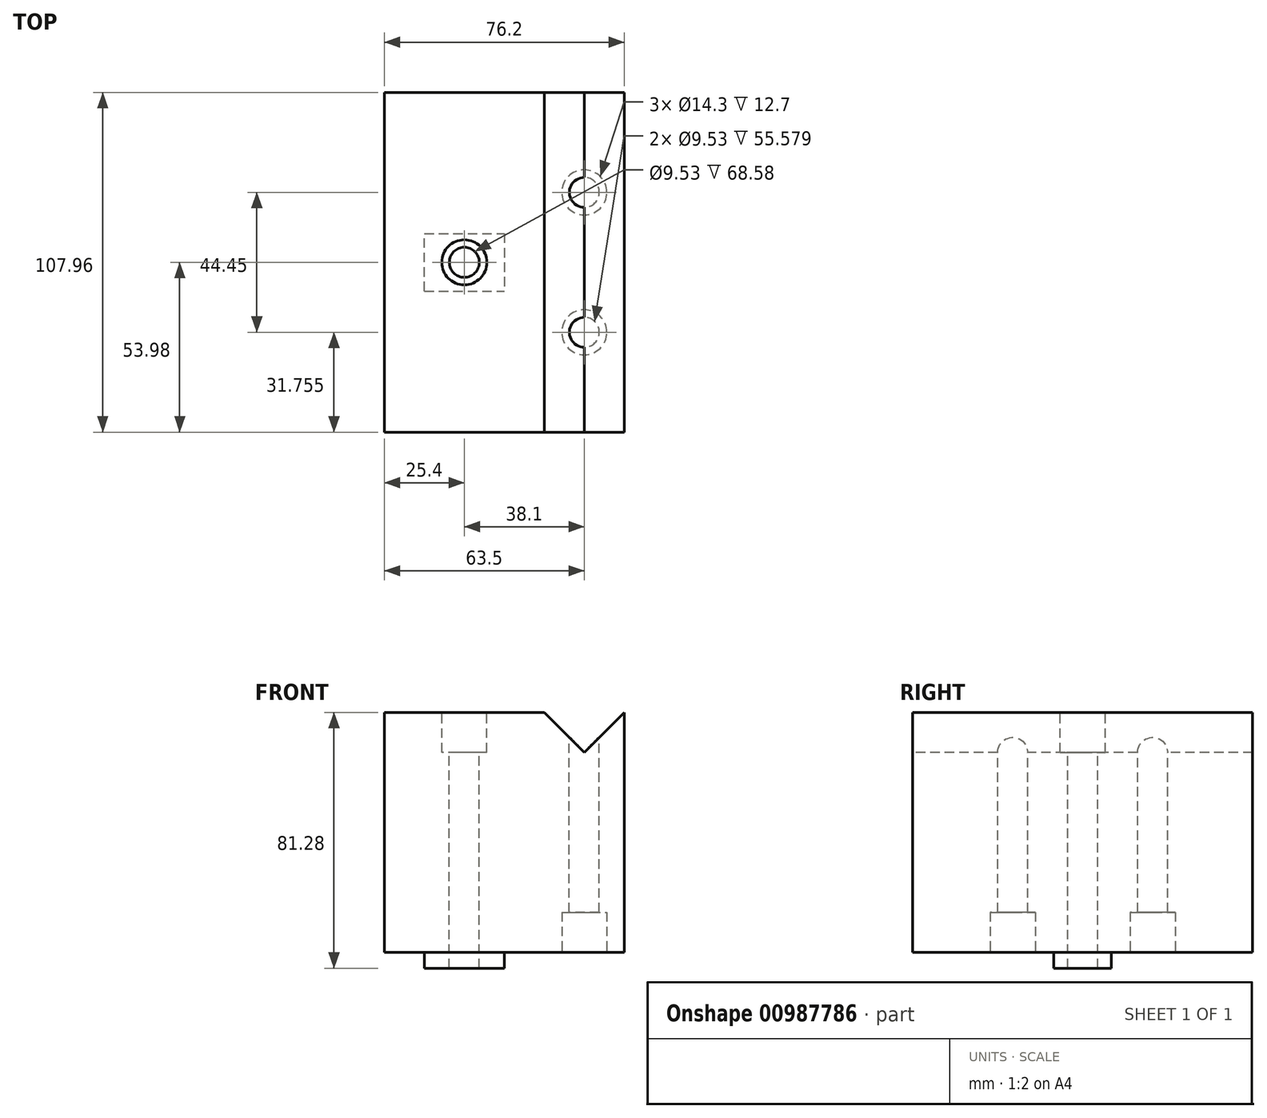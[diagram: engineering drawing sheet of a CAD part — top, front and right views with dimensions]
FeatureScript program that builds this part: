
annotation { "Feature Type Name" : "Feature", "Feature Type Description" : "" }
export const myFeature = defineFeature(function(context is Context, id is Id, definition is map)
    precondition{}
    {
        {
            var Q0;
            Q0=qCreatedBy(makeId("Front.planeOp"),FACE);
            var sketch = newSketch(context, id + "F0", { "sketchPlane" : qUnion([Q0])});
            skLineSegment(sketch, "E0.bottom", {"start": v(-38.1, 0) * mm, "end": v(38.1, 0) * mm});
            skLineSegment(sketch, "E0.top", {"start": v(-38.1, 76.2) * mm, "end": v(38.1, 76.2) * mm});
            skLineSegment(sketch, "E0.left", {"start": v(-38.1, 0) * mm, "end": v(-38.1, 76.2) * mm});
            skLineSegment(sketch, "E0.right", {"start": v(38.1, 0) * mm, "end": v(38.1, 76.2) * mm});
            skSolve(sketch);
        }
        {
            var Q0;
            Q0=makeQuery(id+"F0.imprint","IMPRINT",FACE,{"disambiguationData":[TD([[makeQuery(id+"F0.imprint","IMPRINT",EDGE,{"derivedFrom":sQuery(id+"F0.wireOp",EDGE,"E0.bottom")}),1.0]])]});
            extrude(context, id + "F1", {"entities" : qUnion([Q0]), "endBound" : BoundingType.SYMMETRIC, "depth" : 107.95 * mm, "offsetDistance" : 25 * mm});
        }
        {
            var Q0;
            Q0=makeQuery(id+"F1.opExtrude","CAP_FACE",FACE,{"disambiguationData":[OSD([sQuery(id+"F0.wireOp",EDGE,"E0.bottom"),sQuery(id+"F0.wireOp",EDGE,"E0.top"),sQuery(id+"F0.wireOp",EDGE,"E0.left"),sQuery(id+"F0.wireOp",EDGE,"E0.right")])],"isStart":false});
            var sketch = newSketch(context, id + "F2", { "sketchPlane" : qUnion([Q0])});
            skLineSegment(sketch, "E1", {"start": v(12.7, 76.2) * mm, "end": v(25.4, 63.5) * mm});
            skLineSegment(sketch, "E2", {"start": v(25.4, 63.5) * mm, "end": v(38.1, 76.2) * mm});
            skLineSegment(sketch, "E3", {"start": v(12.7, 76.2) * mm, "end": v(38.1, 76.2) * mm});
            skSolve(sketch);
        }
        {
            var Q0;
            Q0 = qSketchRegion(id + "F2", true);
            extrude(context, id + "F3", {"entities" : qUnion([Q0]), "operationType" : NewBodyOperationType.REMOVE, "endBound" : BoundingType.THROUGH_ALL, "oppositeDirection" : true, "depth" : 25 * mm, "offsetDistance" : 25 * mm});
        }
        {
            var Q0;
            Q0=makeQuery(id+"F1.opExtrude","SWEPT_FACE",FACE,{"disambiguationData":[OSD([sQuery(id+"F0.wireOp",EDGE,"E0.top")])]});
            var sketch = newSketch(context, id + "F4", { "sketchPlane" : qUnion([Q0])});
            skCircle(sketch, "E4", {"center": v(25.4, 22.22) * mm, "radius": 4.76 * mm});
            skCircle(sketch, "E5", {"center": v(25.4, -22.22) * mm, "radius": 4.76 * mm});
            skCircle(sketch, "E6", {"center": v(-12.7, 0) * mm, "radius": 4.76 * mm});
            skSolve(sketch);
        }
        {
            var Q0;
            Q0=makeQuery(id+"F1.opExtrude","SWEPT_FACE",FACE,{"disambiguationData":[OSD([sQuery(id+"F0.wireOp",EDGE,"E0.right")])]});
            var sketch = newSketch(context, id + "F5", { "sketchPlane" : qUnion([Q0])});
            skLineSegment(sketch, "E7.bottom", {"start": v(-9.14, 0) * mm, "end": v(9.14, 0) * mm});
            skLineSegment(sketch, "E7.top", {"start": v(-9.14, -5.08) * mm, "end": v(9.14, -5.08) * mm});
            skLineSegment(sketch, "E7.left", {"start": v(-9.14, 0) * mm, "end": v(-9.14, -5.08) * mm});
            skLineSegment(sketch, "E7.right", {"start": v(9.14, 0) * mm, "end": v(9.14, -5.08) * mm});
            skSolve(sketch);
        }
        {
            var Q0;
            Q0 = qSketchRegion(id + "F5", true);
            var Q1;
            Q1=makeQuery(id+"F1.opExtrude","SWEPT_FACE",FACE,{"disambiguationData":[OSD([sQuery(id+"F0.wireOp",EDGE,"E0.left")])]});
            extrude(context, id + "F6", {"entities" : qUnion([Q0]), "operationType" : NewBodyOperationType.ADD, "oppositeDirection" : true, "depth" : 63.5 * mm, "endBoundEntityFace" : qUnion([Q1]), "offsetDistance" : 25 * mm});
        }
        {
            var Q0;
            Q0 = qSketchRegion(id + "F4", true);
            extrude(context, id + "F7", {"entities" : qUnion([Q0]), "operationType" : NewBodyOperationType.REMOVE, "endBound" : BoundingType.THROUGH_ALL, "oppositeDirection" : true, "depth" : 25 * mm, "offsetDistance" : 25 * mm});
        }
        {
            var Q0;
            Q0=makeQuery(id+"F1.opExtrude","SWEPT_FACE",FACE,{"disambiguationData":[OSD([sQuery(id+"F0.wireOp",EDGE,"E0.bottom")])]});
            var sketch = newSketch(context, id + "F8", { "sketchPlane" : qUnion([Q0])});
            skCircle(sketch, "E8", {"center": v(25.4, -22.22) * mm, "radius": 7.15 * mm});
            skCircle(sketch, "E9", {"center": v(25.4, 22.22) * mm, "radius": 7.15 * mm});
            skSolve(sketch);
        }
        {
            var Q0;
            Q0 = qSketchRegion(id + "F8", true);
            extrude(context, id + "F9", {"entities" : qUnion([Q0]), "operationType" : NewBodyOperationType.REMOVE, "oppositeDirection" : true, "depth" : 12.7 * mm, "offsetDistance" : 25 * mm});
        }
        {
            var Q0;
            Q0=makeQuery(id+"F1.opExtrude","SWEPT_FACE",FACE,{"disambiguationData":[OSD([sQuery(id+"F0.wireOp",EDGE,"E0.top")])]});
            var sketch = newSketch(context, id + "F10", { "sketchPlane" : qUnion([Q0])});
            skCircle(sketch, "E10", {"center": v(-12.7, 0) * mm, "radius": 7.15 * mm});
            skSolve(sketch);
        }
        {
            var Q0;
            Q0 = qSketchRegion(id + "F10", true);
            extrude(context, id + "F11", {"entities" : qUnion([Q0]), "operationType" : NewBodyOperationType.REMOVE, "oppositeDirection" : true, "depth" : 12.7 * mm, "offsetDistance" : 25 * mm});
        }
        {
            var Q0;
            Q0=makeQuery(id+"F1.opExtrude","CAP_FACE",FACE,{"disambiguationData":[OSD([sQuery(id+"F0.wireOp",EDGE,"E0.bottom"),sQuery(id+"F0.wireOp",EDGE,"E0.top"),sQuery(id+"F0.wireOp",EDGE,"E0.left"),sQuery(id+"F0.wireOp",EDGE,"E0.right")])],"isStart":false});
            var sketch = newSketch(context, id + "F12", { "sketchPlane" : qUnion([Q0])});
            skLineSegment(sketch, "E11.bottom", {"start": v(38.1, 0) * mm, "end": v(0, 0) * mm});
            skLineSegment(sketch, "E11.top", {"start": v(38.1, -9) * mm, "end": v(0, -9) * mm});
            skLineSegment(sketch, "E11.left", {"start": v(38.1, 0) * mm, "end": v(38.1, -9) * mm});
            skLineSegment(sketch, "E11.right", {"start": v(0, 0) * mm, "end": v(0, -9) * mm});
            skSolve(sketch);
        }
        {
            var Q0;
            Q0 = qSketchRegion(id + "F12", true);
            extrude(context, id + "F13", {"entities" : qUnion([Q0]), "operationType" : NewBodyOperationType.REMOVE, "endBound" : BoundingType.THROUGH_ALL, "oppositeDirection" : true, "depth" : 25 * mm, "offsetDistance" : 25 * mm});
        }
    });
